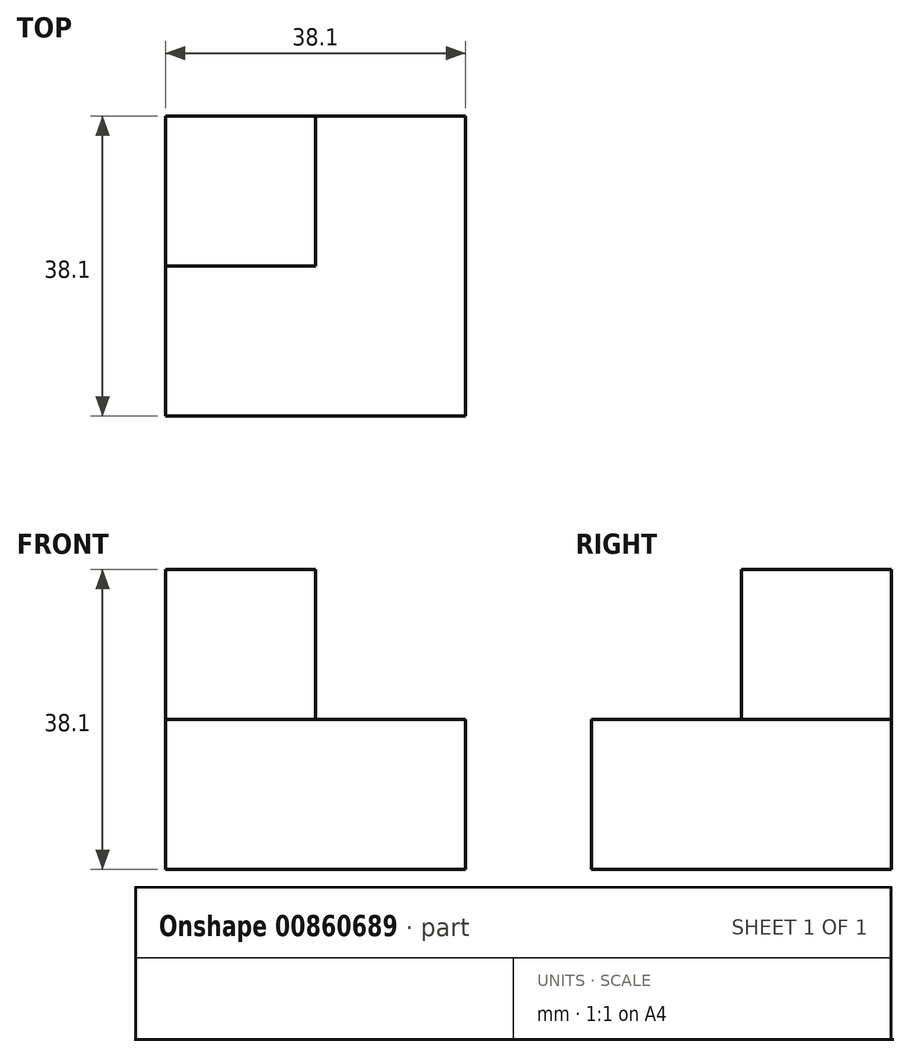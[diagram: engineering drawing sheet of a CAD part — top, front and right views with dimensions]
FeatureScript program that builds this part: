
annotation { "Feature Type Name" : "Feature", "Feature Type Description" : "" }
export const myFeature = defineFeature(function(context is Context, id is Id, definition is map)
    precondition{}
    {
        {
            var Q0;
            Q0=qCreatedBy(makeId("Top.planeOp"),FACE);
            var sketch = newSketch(context, id + "F0", { "sketchPlane" : qUnion([Q0])});
            skLineSegment(sketch, "E0", {"start": v(0, 0) * mm, "end": v(0, 38.1) * mm});
            skLineSegment(sketch, "E1", {"start": v(0, 38.1) * mm, "end": v(38.1, 38.1) * mm});
            skLineSegment(sketch, "E2", {"start": v(38.1, 38.1) * mm, "end": v(38.1, 0) * mm});
            skLineSegment(sketch, "E3", {"start": v(38.1, 0) * mm, "end": v(0, 0) * mm});
            skSolve(sketch);
        }
        {
            var Q0;
            Q0 = qSketchRegion(id + "F0", true);
            extrude(context, id + "F1", {"entities" : qUnion([Q0]), "depth" : 19.05 * mm, "offsetDistance" : 25.4 * mm});
        }
        {
            var Q0;
            Q0=makeQuery(id+"F1.opExtrude","CAP_FACE",FACE,{"disambiguationData":[OSD([sQuery(id+"F0.wireOp",EDGE,"E0"),sQuery(id+"F0.wireOp",EDGE,"E1"),sQuery(id+"F0.wireOp",EDGE,"E2"),sQuery(id+"F0.wireOp",EDGE,"E3")])],"isStart":false});
            var sketch = newSketch(context, id + "F2", { "sketchPlane" : qUnion([Q0])});
            skLineSegment(sketch, "E4", {"start": v(0, 38.1) * mm, "end": v(19.05, 38.1) * mm});
            skLineSegment(sketch, "E5", {"start": v(19.05, 38.1) * mm, "end": v(19.05, 19.05) * mm});
            skLineSegment(sketch, "E6", {"start": v(19.05, 19.05) * mm, "end": v(0, 19.05) * mm});
            skLineSegment(sketch, "E7", {"start": v(0, 19.05) * mm, "end": v(0, 38.1) * mm});
            skSolve(sketch);
        }
        {
            var Q0;
            Q0=makeQuery(id+"F2.imprint","IMPRINT",FACE,{"disambiguationData":[TD([[makeQuery(id+"F2.imprint","IMPRINT",EDGE,{"derivedFrom":sQuery(id+"F2.wireOp",EDGE,"E4")}),-1.0]])]});
            extrude(context, id + "F3", {"entities" : qUnion([Q0]), "operationType" : NewBodyOperationType.ADD, "depth" : 19.05 * mm, "offsetDistance" : 25.4 * mm});
        }
    });
